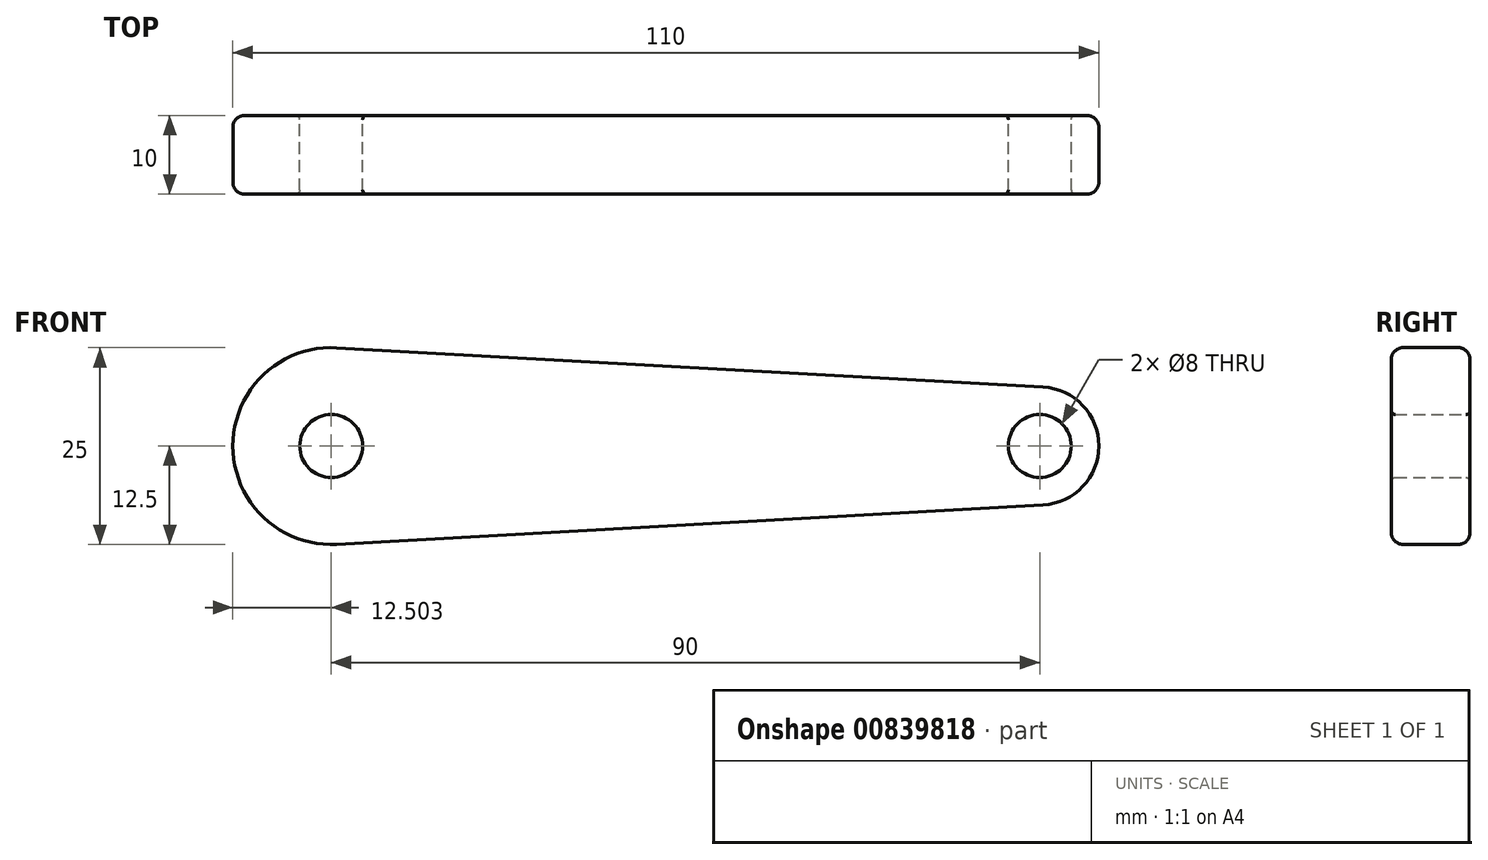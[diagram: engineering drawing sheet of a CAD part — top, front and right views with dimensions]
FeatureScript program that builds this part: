
annotation { "Feature Type Name" : "Feature", "Feature Type Description" : "" }
export const myFeature = defineFeature(function(context is Context, id is Id, definition is map)
    precondition{}
    {
        {
            var Q0;
            Q0=qCreatedBy(makeId("Front.planeOp"),FACE);
            var sketch = newSketch(context, id + "F0", { "sketchPlane" : qUnion([Q0])});
            skCircle(sketch, "E0", {"center": v(-46.15, 0) * mm, "radius": 12.5 * mm});
            skCircle(sketch, "E1", {"center": v(43.85, 0) * mm, "radius": 7.5 * mm});
            skCircle(sketch, "E2", {"center": v(-46.15, 0) * mm, "radius": 4 * mm});
            skCircle(sketch, "E3", {"center": v(43.85, 0) * mm, "radius": 4 * mm});
            skLineSegment(sketch, "E4", {"start": v(-45.45, 12.48) * mm, "end": v(44.27, 7.49) * mm});
            skLineSegment(sketch, "E5", {"start": v(-45.45, -12.48) * mm, "end": v(44.27, -7.49) * mm});
            skSolve(sketch);
        }
        {
            var Q0;
            {var subQ0=sQuery(id+"F0.wireOp",EDGE,"E4");Q0=makeQuery(id+"F0.imprint","IMPRINT",FACE,{"disambiguationData":[TD([[makeQuery(id+"F0.imprint","IMPRINT",EDGE,{"derivedFrom":subQ0}),-1.0]])]});}
            var Q1;
            Q1=makeQuery(id+"F0.imprint","IMPRINT",FACE,{"disambiguationData":[TD([[makeQuery(id+"F0.imprint","IMPRINT",EDGE,{"derivedFrom":sQuery(id+"F0.wireOp",EDGE,"E3")}),-1.0]])]});
            var Q2;
            Q2=makeQuery(id+"F0.imprint","IMPRINT",FACE,{"disambiguationData":[TD([[makeQuery(id+"F0.imprint","IMPRINT",EDGE,{"derivedFrom":sQuery(id+"F0.wireOp",EDGE,"E2")}),-1.0]])]});
            extrude(context, id + "F1", {"entities" : qUnion([Q0, Q1, Q2]), "depth" : 10 * mm, "offsetDistance" : 25 * mm});
        }
        {
            var Q0;
            Q0=makeQuery(id+"F1.opExtrude","CAP_EDGE",EDGE,{"disambiguationData":[OSD([sQuery(id+"F0.wireOp",EDGE,"E5")])],"isStart":false});
            var Q1;
            Q1=makeQuery(id+"F1.opExtrude","CAP_EDGE",EDGE,{"disambiguationData":[OSD([sQuery(id+"F0.wireOp",EDGE,"E5")])],"isStart":true});
            fillet(context, id + "F2", {"entities" : qUnion([Q0, Q1]), "radius" : 1.5 * mm, "tangentPropagation" : true, "allowEdgeOverflow" : false});
        }
        {
            var Q0;
            Q0=makeQuery(id+"F1.opExtrude","CAP_EDGE",EDGE,{"disambiguationData":[OSD([sQuery(id+"F0.wireOp",EDGE,"E2")])],"isStart":true});
            var Q1;
            Q1=makeQuery(id+"F1.opExtrude","CAP_EDGE",EDGE,{"disambiguationData":[OSD([sQuery(id+"F0.wireOp",EDGE,"E2")])],"isStart":false});
            var Q2;
            Q2=makeQuery(id+"F1.opExtrude","CAP_EDGE",EDGE,{"disambiguationData":[OSD([sQuery(id+"F0.wireOp",EDGE,"E3")])],"isStart":true});
            var Q3;
            Q3=makeQuery(id+"F1.opExtrude","CAP_EDGE",EDGE,{"disambiguationData":[OSD([sQuery(id+"F0.wireOp",EDGE,"E3")])],"isStart":false});
            fillet(context, id + "F3", {"entities" : qUnion([Q0, Q1, Q2, Q3]), "radius" : 0.5 * mm, "tangentPropagation" : true, "allowEdgeOverflow" : false});
        }
    });
